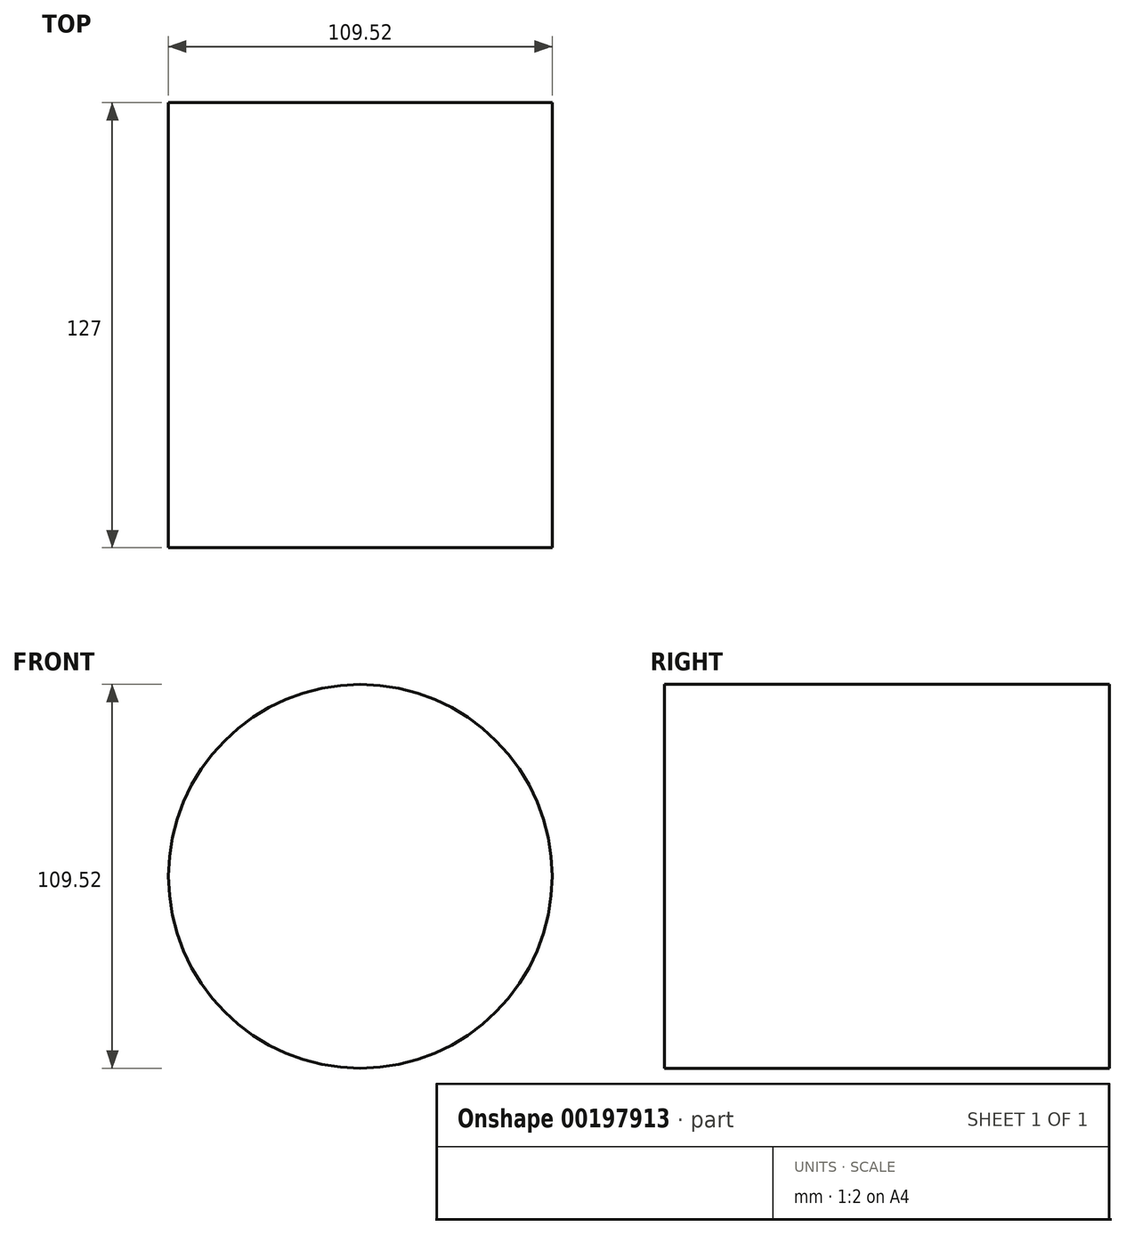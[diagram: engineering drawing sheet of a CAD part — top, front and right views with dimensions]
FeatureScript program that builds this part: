
annotation { "Feature Type Name" : "Feature", "Feature Type Description" : "" }
export const myFeature = defineFeature(function(context is Context, id is Id, definition is map)
    precondition{}
    {
        {
            var Q0;
            Q0=qCreatedBy(makeId("Front.planeOp"),FACE);
            var sketch = newSketch(context, id + "F0", { "sketchPlane" : qUnion([Q0])});
            skCircle(sketch, "E0", {"center": v(0, 0) * mm, "radius": 54.76 * mm});
            skSolve(sketch);
        }
        {
            var Q0;
            Q0=sQuery(id+"F0.wireOp",EDGE,"E0");
            extrude(context, id + "F1", {"bodyType" : ToolBodyType.SURFACE, "surfaceEntities" : qUnion([Q0]), "depth" : 127 * mm});
        }
    });
